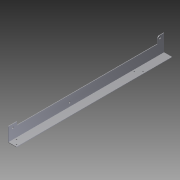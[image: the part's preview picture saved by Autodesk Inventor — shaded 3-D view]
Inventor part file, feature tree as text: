
AUTODESK INVENTOR PART (.ipt)
format: ipt  version: 2012 (Build 160160000, 160)  size: 123,392 bytes
history: native  units: in
note: dims shown in document units (in); Inventor stores cm internally (conversion verified against a paired STEP export)
features: extrude x3, sketch x3
ambient origin geometry x8: Origin, YZ Plane, XZ Plane, XY Plane, X Axis, Y Axis, Z Axis, Center Point
bodies: Solid1 (feature_tree)
feature tree (6):
  extrude  "Extrusion1"  Depth=0.0625in
  extrude  "Extrusion2"  Depth=2.0in
  extrude  "Extrusion3"  Depth=0.75in
  sketch  "Sketch1"  dims[d0=0.0625in d1=0.0625in]
  sketch  "Sketch2"  dims[d2=1.0in d3=2.0in]
  sketch  "Sketch3"  dims[d4=18.0in d5=0.0in d6=0.75in d7=0.75in d8=0.25in d9=0.5in d10=0.25in d11=1.0in d12=0.0in d13=0.875in d14=1.0in d15=0.2in d16=1.25in d17=0.5in d18=0.375in d19=0.5in d20=0.125in d21=0.25in d22=0.25in d24=3.125in d25=1.0in d26=0.0in d27=7.5in d28=0.25in d29=0.25in d30=0.5in]
